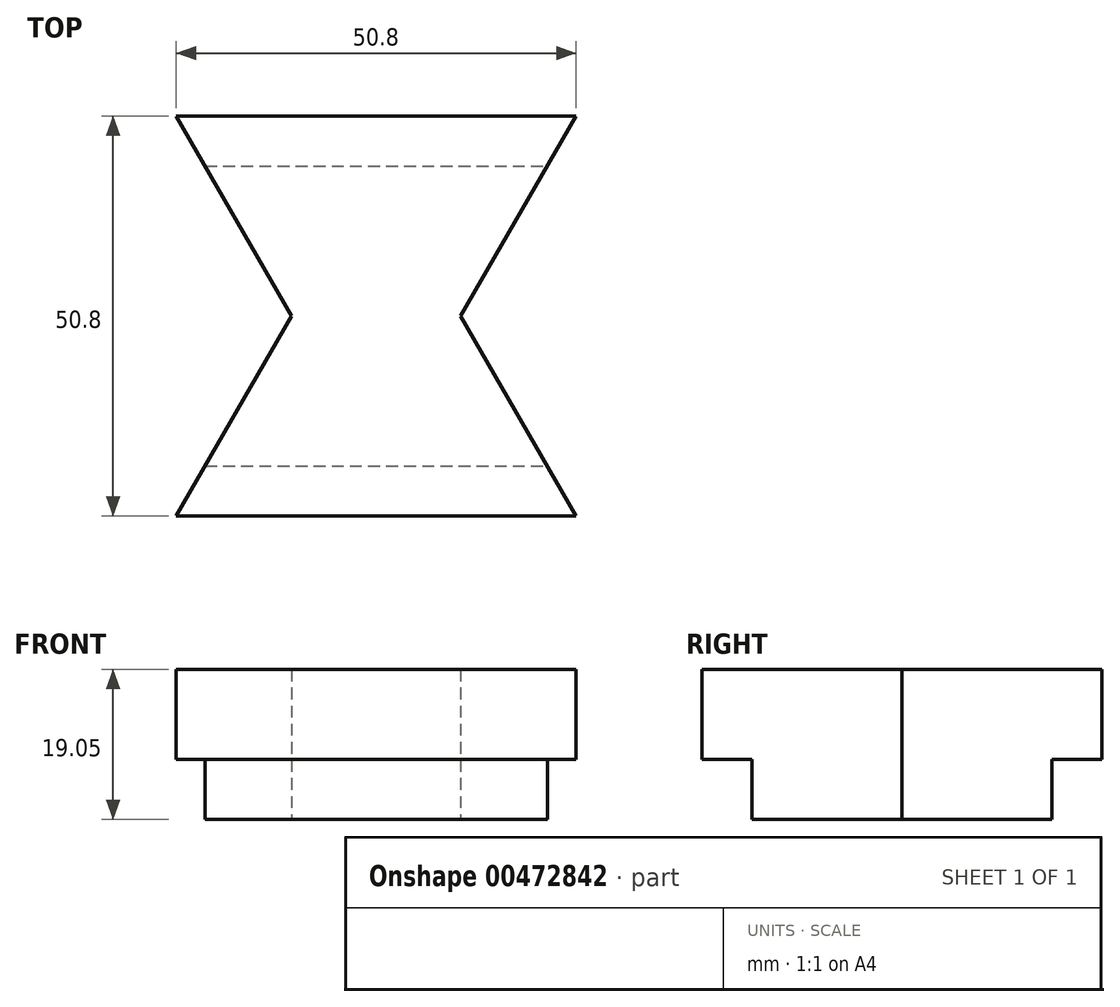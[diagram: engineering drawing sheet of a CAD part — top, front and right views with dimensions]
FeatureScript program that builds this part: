
annotation { "Feature Type Name" : "Feature", "Feature Type Description" : "" }
export const myFeature = defineFeature(function(context is Context, id is Id, definition is map)
    precondition{}
    {
        {
            var Q0;
            Q0=qCreatedBy(makeId("Top.planeOp"),FACE);
            var sketch = newSketch(context, id + "F0", { "sketchPlane" : qUnion([Q0])});
            skLineSegment(sketch, "E0", {"start": v(0, 0) * mm, "end": v(-25.4, 0) * mm});
            skLineSegment(sketch, "E1", {"start": v(-25.4, 0) * mm, "end": v(-10.74, -25.4) * mm});
            skLineSegment(sketch, "E2.MirrorCS", {"start": v(0, 0) * mm, "end": v(25.4, 0) * mm});
            skLineSegment(sketch, "E3.MirrorCS", {"start": v(25.4, 0) * mm, "end": v(10.74, -25.4) * mm});
            skLineSegment(sketch, "E4", {"start": v(-10.74, -25.4) * mm, "end": v(10.74, -25.4) * mm, "construction": true});
            skLineSegment(sketch, "E5.MirrorCS", {"start": v(-25.4, -50.8) * mm, "end": v(-10.74, -25.4) * mm});
            skLineSegment(sketch, "E6.MirrorCS", {"start": v(0, -50.8) * mm, "end": v(-25.4, -50.8) * mm});
            skLineSegment(sketch, "E7.MirrorCS", {"start": v(0, -50.8) * mm, "end": v(25.4, -50.8) * mm});
            skLineSegment(sketch, "E8.MirrorCS", {"start": v(25.4, -50.8) * mm, "end": v(10.74, -25.4) * mm});
            skSolve(sketch);
        }
        {
            var Q0;
            Q0=makeQuery(id+"F0.imprint","IMPRINT",FACE,{"disambiguationData":[TD([[makeQuery(id+"F0.imprint","IMPRINT",EDGE,{"derivedFrom":sQuery(id+"F0.wireOp",EDGE,"E0")}),1.0]])]});
            extrude(context, id + "F1", {"entities" : qUnion([Q0]), "depth" : 19.05 * mm});
        }
        {
            var Q0;
            Q0=qCreatedBy(makeId("Right.planeOp"),FACE);
            var sketch = newSketch(context, id + "F2", { "sketchPlane" : qUnion([Q0])});
            skLineSegment(sketch, "E9.bottom", {"start": v(0, 0) * mm, "end": v(-6.35, 0) * mm});
            skLineSegment(sketch, "E9.top", {"start": v(0, 7.62) * mm, "end": v(-6.35, 7.62) * mm});
            skLineSegment(sketch, "E9.left", {"start": v(0, 0) * mm, "end": v(0, 7.62) * mm});
            skLineSegment(sketch, "E9.right", {"start": v(-6.35, 0) * mm, "end": v(-6.35, 7.62) * mm});
            skLineSegment(sketch, "E10.MirrorCS", {"start": v(-50.8, 7.62) * mm, "end": v(-44.45, 7.62) * mm});
            skLineSegment(sketch, "E11.MirrorCS", {"start": v(-44.45, 0) * mm, "end": v(-44.45, 7.62) * mm});
            skLineSegment(sketch, "E12.MirrorCS", {"start": v(-50.8, 0) * mm, "end": v(-44.45, 0) * mm});
            skLineSegment(sketch, "E13.MirrorCS", {"start": v(-50.8, 0) * mm, "end": v(-50.8, 7.62) * mm});
            skSolve(sketch);
        }
        {
            var Q0;
            Q0 = qSketchRegion(id + "F2", true);
            extrude(context, id + "F3", {"entities" : qUnion([Q0]), "operationType" : NewBodyOperationType.REMOVE, "endBound" : BoundingType.UP_TO_NEXT, "oppositeDirection" : true, "depth" : 25.4 * mm, "hasSecondDirection" : true, "secondDirectionOppositeDirection" : false, "secondDirectionDepth" : 25.4 * mm});
        }
    });
